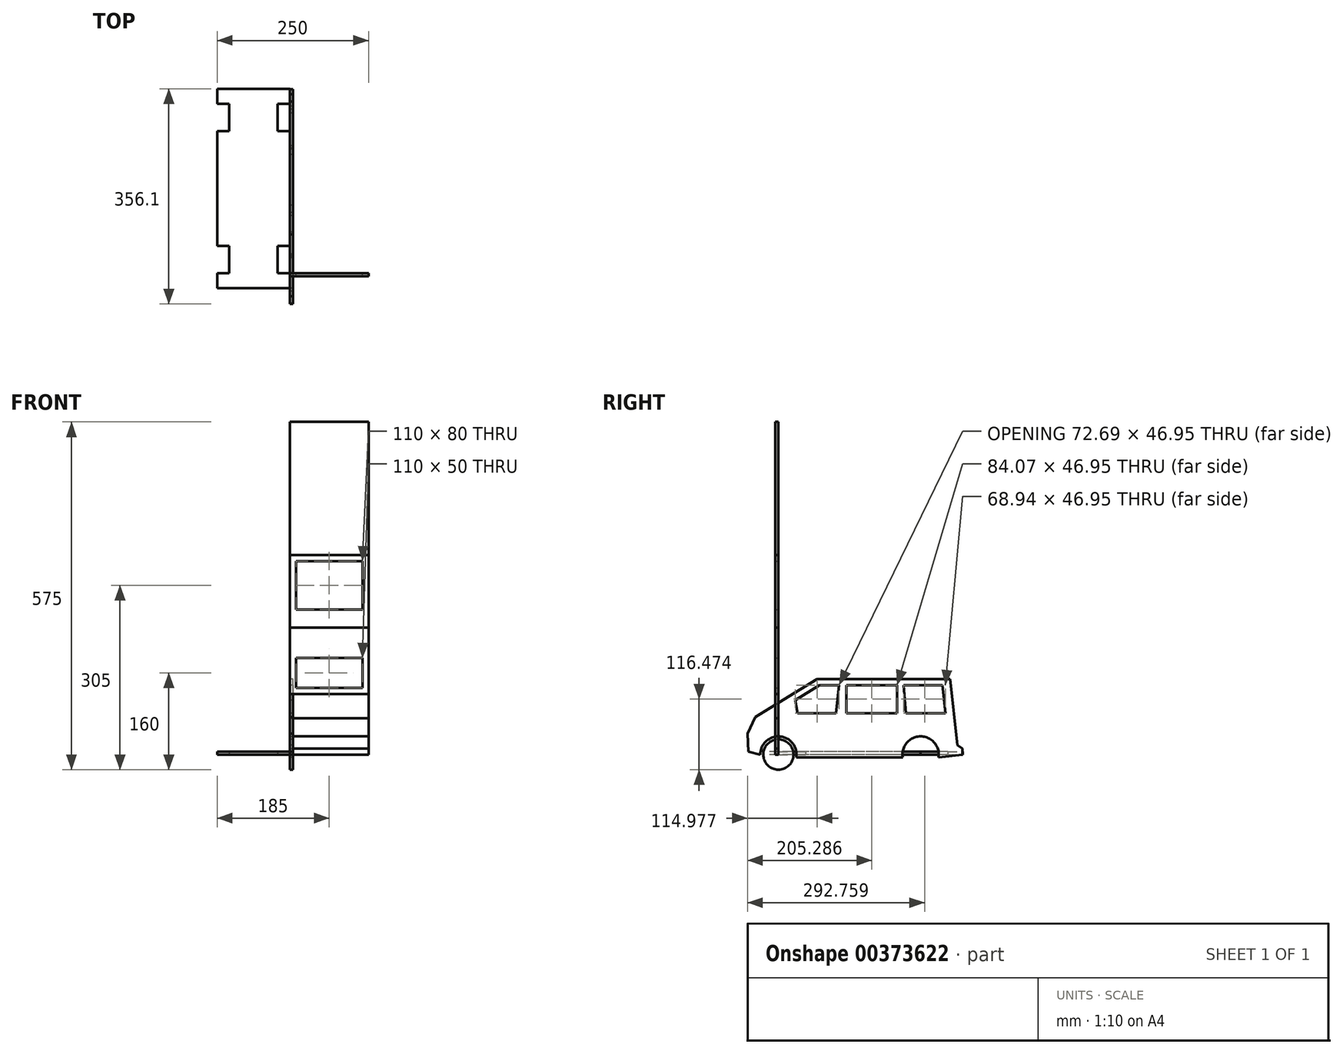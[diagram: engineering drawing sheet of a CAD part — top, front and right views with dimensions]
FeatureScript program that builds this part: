
annotation { "Feature Type Name" : "Feature", "Feature Type Description" : "" }
export const myFeature = defineFeature(function(context is Context, id is Id, definition is map)
    precondition{}
    {
        {
            var Q0;
            Q0=qCreatedBy(makeId("Right.planeOp"),FACE);
            var sketch = newSketch(context, id + "F0", { "sketchPlane" : qUnion([Q0])});
            skCircle(sketch, "E0", {"center": v(0, 0) * mm, "radius": 25 * mm});
            skLineSegment(sketch, "E1", {"start": v(29.58, -5) * mm, "end": v(205.42, -5) * mm});
            skArc(sketch, "E2", {"start": v(29.58, -5) * mm, "mid": v(2.5, 29.9) * mm, "end": v(-30, 0) * mm});
            skArc(sketch, "E3", {"start": v(264.58, -5) * mm, "mid": v(235, 30) * mm, "end": v(205.42, -5) * mm});
            skLineSegment(sketch, "E4", {"start": v(264.58, -5) * mm, "end": v(304.27, 0) * mm});
            skLineSegment(sketch, "E5", {"start": v(304.27, 0) * mm, "end": v(304.27, 10) * mm});
            skLineSegment(sketch, "E6", {"start": v(304.27, 10) * mm, "end": v(296.02, 15.66) * mm});
            skLineSegment(sketch, "E7", {"start": v(-30, 0) * mm, "end": v(-49.36, 5) * mm});
            skPoint(sketch, "E7.endSnap0", {"position": v(304.27, 5) * mm});
            skLineSegment(sketch, "E8", {"start": v(-49.36, 5) * mm, "end": v(-51.1, 34.95) * mm});
            skLineSegment(sketch, "E9", {"start": v(31.6, 68) * mm, "end": v(95.43, 68) * mm});
            skLineSegment(sketch, "E10", {"start": v(95.43, 68) * mm, "end": v(100.22, 114.95) * mm});
            skLineSegment(sketch, "E11", {"start": v(100.22, 114.95) * mm, "end": v(68.07, 114.95) * mm});
            skLineSegment(sketch, "E12", {"start": v(68.07, 114.95) * mm, "end": v(27.53, 89.94) * mm});
            skLineSegment(sketch, "E13", {"start": v(27.53, 89.94) * mm, "end": v(31.6, 68) * mm});
            skLineSegment(sketch, "E14", {"start": v(112.15, 114.95) * mm, "end": v(112.15, 68) * mm});
            skLineSegment(sketch, "E15", {"start": v(112.15, 68) * mm, "end": v(196.22, 68) * mm});
            skLineSegment(sketch, "E16", {"start": v(276.13, 68) * mm, "end": v(270.97, 114.95) * mm});
            skLineSegment(sketch, "E17", {"start": v(270.97, 114.95) * mm, "end": v(207.19, 114.95) * mm});
            skLineSegment(sketch, "E18", {"start": v(64, 125) * mm, "end": v(284, 125) * mm});
            skLineSegment(sketch, "E19", {"start": v(-51.1, 34.95) * mm, "end": v(-38.13, 62) * mm});
            skLineSegment(sketch, "E20", {"start": v(-38.13, 62) * mm, "end": v(64, 125) * mm});
            skLineSegment(sketch, "E21", {"start": v(296.02, 15.66) * mm, "end": v(284, 125) * mm});
            skLineSegment(sketch, "E22", {"start": v(196.22, 114.95) * mm, "end": v(196.22, 68) * mm});
            skLineSegment(sketch, "E23", {"start": v(207.19, 114.95) * mm, "end": v(210.66, 68) * mm});
            skLineSegment(sketch, "E24.trimOffspring", {"start": v(196.22, 114.95) * mm, "end": v(112.15, 114.95) * mm});
            skLineSegment(sketch, "E25.trimOffspring", {"start": v(210.66, 68) * mm, "end": v(276.13, 68) * mm});
            skSolve(sketch);
        }
        {
            var Q0;
            Q0 = qSketchRegion(id + "F0", true);
            extrude(context, id + "F1", {"entities" : qUnion([Q0]), "depth" : 5 * mm});
        }
        {
            var Q0;
            Q0=qCreatedBy(makeId("Top.planeOp"),FACE);
            var sketch = newSketch(context, id + "F2", { "sketchPlane" : qUnion([Q0])});
            skLineSegment(sketch, "E26.left", {"start": v(-120, 235) * mm, "end": v(-120, 45) * mm});
            skLineSegment(sketch, "E26.right", {"start": v(0, 235) * mm, "end": v(0, 45) * mm});
            skLineSegment(sketch, "E27", {"start": v(-60, 280) * mm, "end": v(-60, 0) * mm, "construction": true});
            skLineSegment(sketch, "E28", {"start": v(-20, 280) * mm, "end": v(-20, 235) * mm});
            skLineSegment(sketch, "E29", {"start": v(-20, 235) * mm, "end": v(0, 235) * mm});
            skLineSegment(sketch, "E30", {"start": v(-100, 280) * mm, "end": v(-100, 235) * mm});
            skLineSegment(sketch, "E31", {"start": v(-100, 235) * mm, "end": v(-120, 235) * mm});
            skLineSegment(sketch, "E32", {"start": v(-120, 45) * mm, "end": v(-100, 45) * mm});
            skLineSegment(sketch, "E33", {"start": v(-100, 45) * mm, "end": v(-100, 0) * mm});
            skLineSegment(sketch, "E34", {"start": v(-20, 0) * mm, "end": v(-20, 45) * mm});
            skLineSegment(sketch, "E35", {"start": v(-20, 45) * mm, "end": v(0, 45) * mm});
            skPoint(sketch, "E36.orphan", {"position": v(-120, 0) * mm});
            skPoint(sketch, "E37.orphan", {"position": v(0, 0) * mm});
            skPoint(sketch, "E38.orphan", {"position": v(0, 280) * mm});
            skPoint(sketch, "E39.orphan", {"position": v(-120, 280) * mm});
            skLineSegment(sketch, "E40.bottom", {"start": v(-120, 0) * mm, "end": v(-100, 0) * mm});
            skLineSegment(sketch, "E40.top", {"start": v(-120, -25) * mm, "end": v(0, -25) * mm});
            skLineSegment(sketch, "E40.left", {"start": v(-120, 0) * mm, "end": v(-120, -25) * mm});
            skLineSegment(sketch, "E40.right", {"start": v(0, 0) * mm, "end": v(0, -25) * mm});
            skPoint(sketch, "E40.middle", {"position": v(-60, -12.5) * mm});
            skLineSegment(sketch, "E41.bottom", {"start": v(-120, 280) * mm, "end": v(-100, 280) * mm});
            skLineSegment(sketch, "E41.top", {"start": v(-120, 305) * mm, "end": v(0, 305) * mm});
            skLineSegment(sketch, "E41.left", {"start": v(-120, 280) * mm, "end": v(-120, 305) * mm});
            skLineSegment(sketch, "E41.right", {"start": v(0, 280) * mm, "end": v(0, 305) * mm});
            skPoint(sketch, "E41.middle", {"position": v(-60, 292.5) * mm});
            skLineSegment(sketch, "E42.trimOffspring", {"start": v(-20, 280) * mm, "end": v(0, 280) * mm});
            skLineSegment(sketch, "E43.trimOffspring", {"start": v(-20, 0) * mm, "end": v(0, 0) * mm});
            skSolve(sketch);
        }
        {
            var Q0;
            Q0 = qSketchRegion(id + "F2", true);
            extrude(context, id + "F3", {"entities" : qUnion([Q0]), "depth" : 5 * mm});
        }
        {
            var Q0;
            Q0=qCreatedBy(makeId("Front.planeOp"),FACE);
            var sketch = newSketch(context, id + "F4", { "sketchPlane" : qUnion([Q0])});
            skLineSegment(sketch, "E44.bottom", {"start": v(0, 0) * mm, "end": v(130, 0) * mm});
            skLineSegment(sketch, "E44.top", {"start": v(0, 10) * mm, "end": v(130, 10) * mm});
            skLineSegment(sketch, "E44.left", {"start": v(0, 0) * mm, "end": v(0, 10) * mm});
            skLineSegment(sketch, "E44.right", {"start": v(130, 0) * mm, "end": v(130, 10) * mm});
            skLineSegment(sketch, "E45.top", {"start": v(0, 30) * mm, "end": v(130, 30) * mm});
            skLineSegment(sketch, "E45.left", {"start": v(0, 10) * mm, "end": v(0, 30) * mm});
            skLineSegment(sketch, "E45.right", {"start": v(130, 10) * mm, "end": v(130, 30) * mm});
            skLineSegment(sketch, "E46.top", {"start": v(0, 60) * mm, "end": v(130, 60) * mm});
            skLineSegment(sketch, "E46.left", {"start": v(0, 30) * mm, "end": v(0, 60) * mm});
            skLineSegment(sketch, "E46.right", {"start": v(130, 30) * mm, "end": v(130, 60) * mm});
            skLineSegment(sketch, "E47.top", {"start": v(0, 100) * mm, "end": v(130, 100) * mm});
            skLineSegment(sketch, "E47.left", {"start": v(0, 60) * mm, "end": v(0, 100) * mm});
            skLineSegment(sketch, "E47.right", {"start": v(130, 60) * mm, "end": v(130, 100) * mm});
            skLineSegment(sketch, "E48.top", {"start": v(0, 210) * mm, "end": v(130, 210) * mm});
            skLineSegment(sketch, "E48.left", {"start": v(0, 100) * mm, "end": v(0, 210) * mm});
            skLineSegment(sketch, "E48.right", {"start": v(130, 100) * mm, "end": v(130, 210) * mm});
            skLineSegment(sketch, "E49.top", {"start": v(0, 330) * mm, "end": v(130, 330) * mm});
            skLineSegment(sketch, "E49.left", {"start": v(0, 210) * mm, "end": v(0, 330) * mm});
            skLineSegment(sketch, "E49.right", {"start": v(130, 210) * mm, "end": v(130, 330) * mm});
            skLineSegment(sketch, "E50.top", {"start": v(0, 550) * mm, "end": v(130, 550) * mm});
            skLineSegment(sketch, "E50.left", {"start": v(0, 330) * mm, "end": v(0, 550) * mm});
            skLineSegment(sketch, "E50.right", {"start": v(130, 330) * mm, "end": v(130, 550) * mm});
            skLineSegment(sketch, "E51.bottom", {"start": v(10, 320) * mm, "end": v(120, 320) * mm});
            skLineSegment(sketch, "E51.top", {"start": v(10, 240) * mm, "end": v(120, 240) * mm});
            skLineSegment(sketch, "E51.left", {"start": v(10, 320) * mm, "end": v(10, 240) * mm});
            skLineSegment(sketch, "E51.right", {"start": v(120, 320) * mm, "end": v(120, 240) * mm});
            skLineSegment(sketch, "E52.bottom", {"start": v(10, 160) * mm, "end": v(120, 160) * mm});
            skLineSegment(sketch, "E52.top", {"start": v(10, 110) * mm, "end": v(120, 110) * mm});
            skLineSegment(sketch, "E52.left", {"start": v(10, 160) * mm, "end": v(10, 110) * mm});
            skLineSegment(sketch, "E52.right", {"start": v(120, 160) * mm, "end": v(120, 110) * mm});
            skSolve(sketch);
        }
        {
            var Q0;
            Q0=makeQuery(id+"F4.imprint","IMPRINT",FACE,{"disambiguationData":[TD([[makeQuery(id+"F4.imprint","IMPRINT",EDGE,{"derivedFrom":sQuery(id+"F4.wireOp",EDGE,"E49.top")}),1.0]])]});
            extrude(context, id + "F5", {"entities" : qUnion([Q0]), "depth" : 5 * mm});
        }
        {
            var Q0;
            Q0=makeQuery(id+"F4.imprint","IMPRINT",FACE,{"disambiguationData":[TD([[makeQuery(id+"F4.imprint","IMPRINT",EDGE,{"derivedFrom":sQuery(id+"F4.wireOp",EDGE,"E48.top")}),1.0]])]});
            extrude(context, id + "F6", {"entities" : qUnion([Q0]), "depth" : 5 * mm});
        }
        {
            var Q0;
            Q0=makeQuery(id+"F4.imprint","IMPRINT",FACE,{"disambiguationData":[TD([[makeQuery(id+"F4.imprint","IMPRINT",EDGE,{"derivedFrom":sQuery(id+"F4.wireOp",EDGE,"E47.top")}),1.0]])]});
            extrude(context, id + "F7", {"entities" : qUnion([Q0]), "depth" : 5 * mm});
        }
        {
            var Q0;
            Q0=makeQuery(id+"F4.imprint","IMPRINT",FACE,{"disambiguationData":[TD([[makeQuery(id+"F4.imprint","IMPRINT",EDGE,{"derivedFrom":sQuery(id+"F4.wireOp",EDGE,"E46.top")}),1.0]])]});
            extrude(context, id + "F8", {"entities" : qUnion([Q0]), "depth" : 5 * mm});
        }
        {
            var Q0;
            Q0=makeQuery(id+"F4.imprint","IMPRINT",FACE,{"disambiguationData":[TD([[makeQuery(id+"F4.imprint","IMPRINT",EDGE,{"derivedFrom":sQuery(id+"F4.wireOp",EDGE,"E45.top")}),1.0]])]});
            extrude(context, id + "F9", {"entities" : qUnion([Q0]), "depth" : 5 * mm});
        }
        {
            var Q0;
            Q0=makeQuery(id+"F4.imprint","IMPRINT",FACE,{"disambiguationData":[TD([[makeQuery(id+"F4.imprint","IMPRINT",EDGE,{"derivedFrom":sQuery(id+"F4.wireOp",EDGE,"E44.top")}),1.0]])]});
            extrude(context, id + "F10", {"entities" : qUnion([Q0]), "depth" : 5 * mm});
        }
        {
            var Q0;
            Q0=makeQuery(id+"F4.imprint","IMPRINT",FACE,{"disambiguationData":[TD([[makeQuery(id+"F4.imprint","IMPRINT",EDGE,{"derivedFrom":sQuery(id+"F4.wireOp",EDGE,"E44.bottom")}),1.0]])]});
            extrude(context, id + "F11", {"entities" : qUnion([Q0]), "depth" : 5 * mm});
        }
    });
